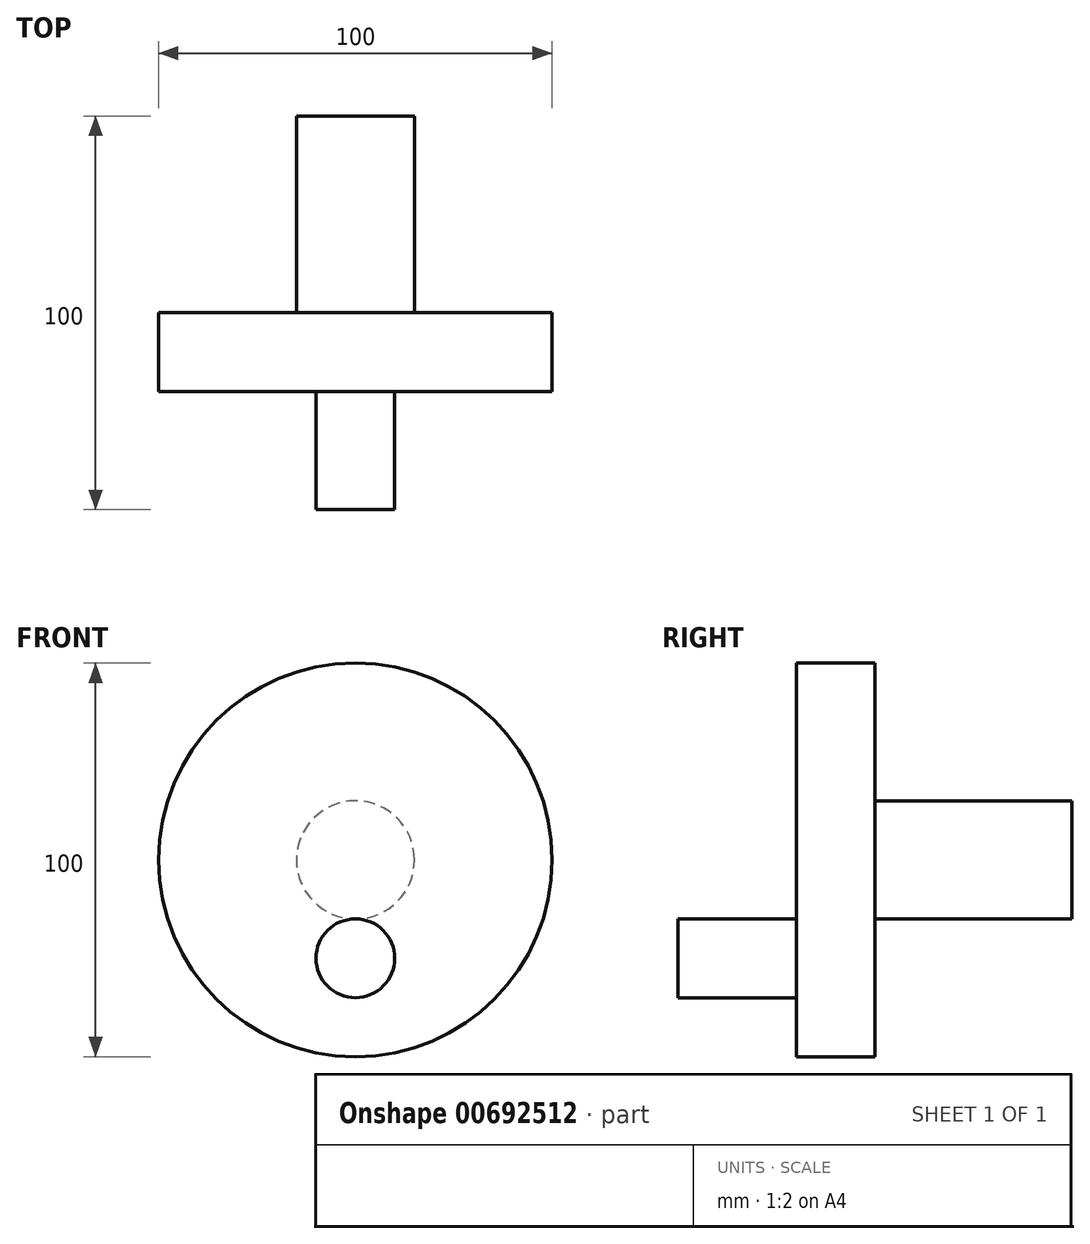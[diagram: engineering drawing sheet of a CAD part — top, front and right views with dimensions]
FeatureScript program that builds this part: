
annotation { "Feature Type Name" : "Feature", "Feature Type Description" : "" }
export const myFeature = defineFeature(function(context is Context, id is Id, definition is map)
    precondition{}
    {
        {
            var Q0;
            Q0=qCreatedBy(makeId("Front.planeOp"),FACE);
            var sketch = newSketch(context, id + "F0", { "sketchPlane" : qUnion([Q0])});
            skCircle(sketch, "E0", {"center": v(0, 0) * mm, "radius": 50 * mm});
            skLineSegment(sketch, "E1", {"start": v(0, 0) * mm, "end": v(0, -25) * mm});
            skCircle(sketch, "E2", {"center": v(0, -25) * mm, "radius": 10 * mm});
            skSolve(sketch);
        }
        {
            var Q0;
            Q0=makeQuery(id+"F0.imprint","IMPRINT",FACE,{"disambiguationData":[TD([[makeQuery(id+"F0.imprint","IMPRINT",EDGE,{"derivedFrom":sQuery(id+"F0.wireOp",EDGE,"E0")}),1.0]])]});
            extrude(context, id + "F1", {"entities" : qUnion([Q0]), "depth" : 20 * mm, "offsetDistance" : 25 * mm});
        }
        {
            var Q0;
            Q0=makeQuery(id+"F0.imprint","IMPRINT",FACE,{"disambiguationData":[TD([[makeQuery(id+"F0.imprint","IMPRINT",EDGE,{"derivedFrom":sQuery(id+"F0.wireOp",EDGE,"E2")}),1.0]])]});
            extrude(context, id + "F2", {"entities" : qUnion([Q0]), "operationType" : NewBodyOperationType.ADD, "depth" : 50 * mm, "offsetDistance" : 25 * mm});
        }
        {
            var Q0;
            Q0=makeQuery(id+"F0.imprint","IMPRINT",FACE,{"disambiguationData":[TD([[makeQuery(id+"F0.imprint","IMPRINT",EDGE,{"derivedFrom":sQuery(id+"F0.wireOp",EDGE,"E0")}),1.0]])]});
            var sketch = newSketch(context, id + "F3", { "sketchPlane" : qUnion([Q0])});
            skCircle(sketch, "E3", {"center": v(0, 0) * mm, "radius": 15 * mm});
            skSolve(sketch);
        }
        {
            var Q0;
            Q0=makeQuery(id+"F3.imprint","IMPRINT",FACE,{"disambiguationData":[TD([[makeQuery(id+"F3.imprint","IMPRINT",EDGE,{"derivedFrom":sQuery(id+"F3.wireOp",EDGE,"E3")}),1.0]])]});
            extrude(context, id + "F4", {"entities" : qUnion([Q0]), "operationType" : NewBodyOperationType.ADD, "oppositeDirection" : true, "depth" : 50 * mm, "offsetDistance" : 25 * mm});
        }
    });
